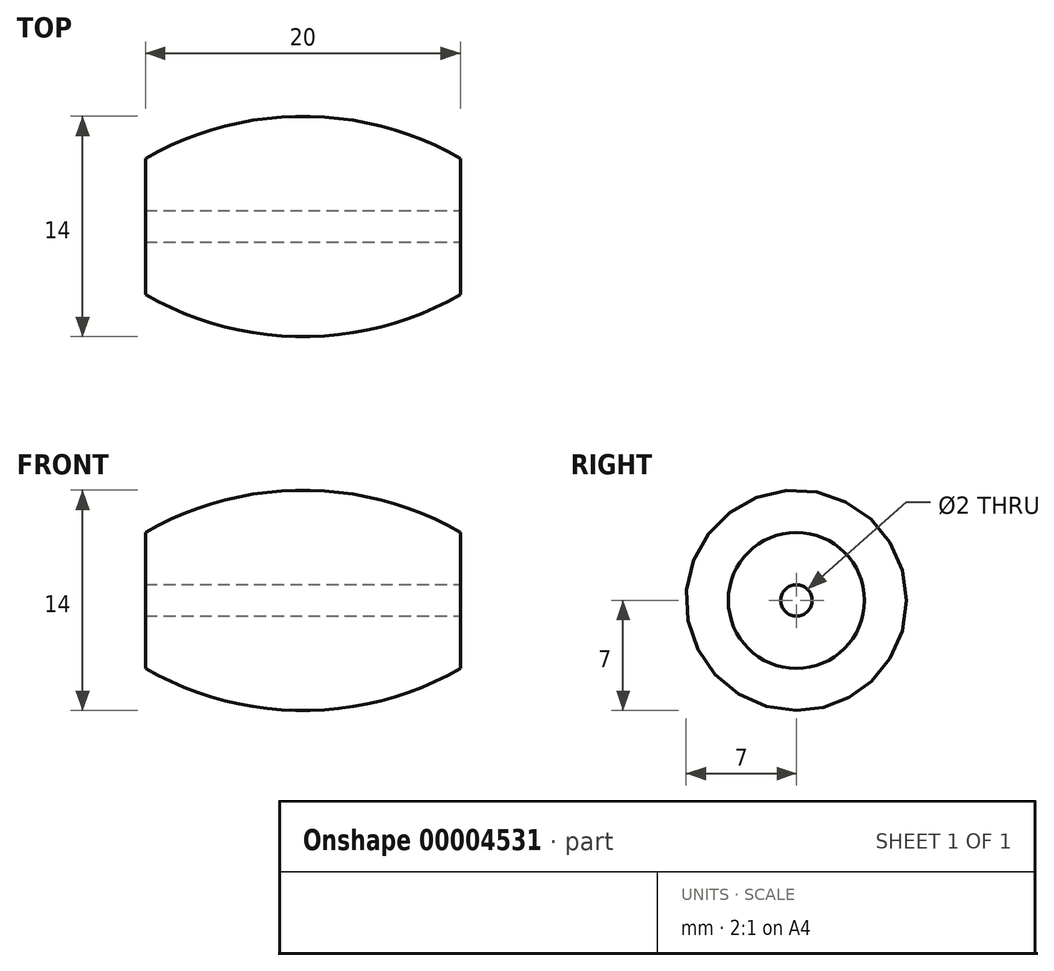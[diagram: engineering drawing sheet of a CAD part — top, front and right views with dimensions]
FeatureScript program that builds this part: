
annotation { "Feature Type Name" : "Feature", "Feature Type Description" : "" }
export const myFeature = defineFeature(function(context is Context, id is Id, definition is map)
    precondition{}
    {
        {
            var Q0;
            Q0=qCreatedBy(makeId("Front.planeOp"),FACE);
            var sketch = newSketch(context, id + "F0", { "sketchPlane" : qUnion([Q0])});
            skLineSegment(sketch, "E0", {"start": v(0, 0) * mm, "end": v(12, 0) * mm, "construction": true});
            skCircle(sketch, "E1", {"center": v(0, 13) * mm, "radius": 20 * mm, "construction": true});
            skLineSegment(sketch, "E2", {"start": v(10, -1) * mm, "end": v(10, -4.32) * mm, "construction": true});
            skLineSegment(sketch, "E3", {"start": v(10, -1) * mm, "end": v(12, -1) * mm, "construction": true});
            skLineSegment(sketch, "E4", {"start": v(12, -1) * mm, "end": v(12, 0) * mm, "construction": true});
            skLineSegment(sketch, "E5", {"start": v(0, 0) * mm, "end": v(0, -7) * mm, "construction": true});
            skLineSegment(sketch, "E6.0.MirrorCS", {"start": v(-10, -1) * mm, "end": v(-12, -1) * mm, "construction": true});
            skLineSegment(sketch, "E6.1.MirrorCS", {"start": v(-10, -1) * mm, "end": v(-10, -4.32) * mm, "construction": true});
            skLineSegment(sketch, "E6.2.MirrorCS", {"start": v(0, 0) * mm, "end": v(-12, 0) * mm, "construction": true});
            skLineSegment(sketch, "E6.3.MirrorCS", {"start": v(-12, -1) * mm, "end": v(-12, 0) * mm, "construction": true});
            skSolve(sketch);
        }
        {
            var Q0;
            Q0=qCreatedBy(makeId("Front.planeOp"),FACE);
            var sketch = newSketch(context, id + "F1", { "sketchPlane" : qUnion([Q0])});
            skLineSegment(sketch, "E7.0", {"start": v(-10, -1) * mm, "end": v(-10, -4.32) * mm});
            skLineSegment(sketch, "E7.7", {"start": v(10, -1) * mm, "end": v(10, -4.32) * mm});
            skArc(sketch, "E8", {"start": v(-10, -4.32) * mm, "mid": v(0, -7) * mm, "end": v(10, -4.32) * mm});
            skLineSegment(sketch, "E9", {"start": v(-10, -1) * mm, "end": v(10, -1) * mm});
            skSolve(sketch);
        }
        {
            var Q0;
            Q0=makeQuery(id+"F1.imprint","IMPRINT",FACE,{"disambiguationData":[TD([[makeQuery(id+"F1.imprint","IMPRINT",EDGE,{"derivedFrom":sQuery(id+"F1.wireOp",EDGE,"E7.0")}),1.0]])]});
            var Q1;
            Q1=sQuery(id+"F0.wireOp",EDGE,"E6.2.MirrorCS");
            revolve(context, id + "F2", {"entities" : qUnion([Q0]), "axis" : qUnion([Q1]), "revolveType" : RevolveType.FULL});
        }
    });
